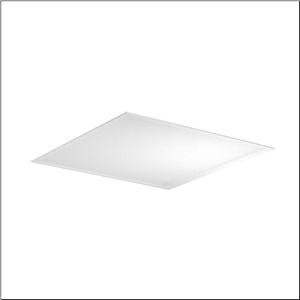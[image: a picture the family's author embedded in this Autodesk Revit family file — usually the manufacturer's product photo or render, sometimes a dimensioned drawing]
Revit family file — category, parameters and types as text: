
# Revit family: apollon_r__21_square_51mq12w72414_a86f
name_source: partatom
category: Lighting Fixtures
units: mm (PartAtom-declared; Revit-internal decimal feet)

## family parameters
Cut with Voids When Loaded = No
Host = Face
Light Source = No
Part Type = Normal
Room Calculation Point = No
Round Connector Dimension = Use Diameter
Shared = No

## types (1)
- Apollon® 21 square (1 x LED, 4200 lm, 23.3 W, 4000K)
    Apparent Load = 23 VA
    CIE Flux Codes = 60 87 97 100 100
    Color Rendering = 80
    Color Temperature = 4000K
    Default Elevation = 1800 mm
    Description = Apollon® 21 square, office luminaire, primary optical cover: micro prismatic cover, of PMMA, CAT 2 (L<= 3000cd/m²), light emission: direct distribution, primary light characteristic: symmetric, installation type: lay-in mounting, LED, rated luminous flux: 4.200lm, luminous efficacy: 180lm/W, light colour: 840, colour temperature: 4000K, with terminal, 3-pole, mains connection: 220..240V, AC/DC, 0/50..60Hz, rated input power: 23W, housing, of aluminium, coated, traffic white (RAL 9016), module: M600, length: 595mm, width: 595mm, height: 30mm, housing upper side, of sheet steel, galvanised, protection rating (complete): IP20, protection rating (lamp compartment, on room side): IP50, insulation class (complete): insulation class II (safety insulation), certification: CE, ENEC, impact resistance: IK03, permissible operating ambient temperature: -20..+45°C, permissible storage temperature: -40..+80°C, packaging unit: 1 piece
    Height = 0 mm  [stored 0 ft]
    Lamp = 1 x LED
    Lamp Light Flux = 4200 lm
    Lamp Power = 23.3 W
    Lamp count = 1
    Length = 595 mm
    Luminous efficacy = 180 lm/W
    Manufacturer = Siteco
    ModVariant = No
    Model = 51MQ12W72414
    Mounting Place = Ceiling
    Mounting Type = Recessed
    Number of Poles = 1
    OnlyDefault = Yes
    Power Factor = 1
    Product Name = Apollon® 21 square
    Product group = office luminaire | ceiling recessed
    ProductGroupID = 401
    Protection Class = Protection class II
    Protection Degree = IP 20
    RLX_Detail_Level = 1
    RLX_Emergency_Light_Flux = 0 lm
    RLX_Emergency_Type = 0
    RLX_Emergency_Type_DB = No
    RlxData = <blob elided: 12485 chars, md5=7ee59517>
    Socket = socket
    Standby Power = 0 W
    System Light Flux = 4200 lm
    System Power = 23 W
    Type Comments = Product without accessories
    Type Image = l_1291049.jpg
    URL = http://relux.com
    VarID = ---
    Voltage = 0 V
    Weight = 0.00 kg
    Width = 595 mm

note: [stored X ft] marks values corroborated as IEEE doubles in the binary element streams (Revit-internal decimal feet)

## geometry (parser evidence)
native form markers: Sweep x9
no freeform markers — native parametric forms only
